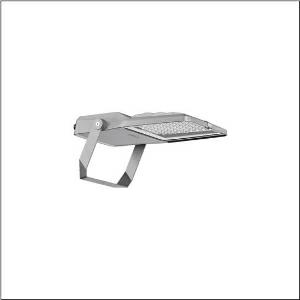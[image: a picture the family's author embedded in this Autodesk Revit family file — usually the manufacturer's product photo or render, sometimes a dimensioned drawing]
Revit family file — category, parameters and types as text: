
# Revit family: floodlight_fl_21_iq_mini___pl52_5xa7772b2d1a_4cc7
name_source: partatom
category: Lighting Fixtures
units: mm (PartAtom-declared; Revit-internal decimal feet)

## family parameters
Cut with Voids When Loaded = No
Host = Face
Light Source = No
Part Type = Normal
Room Calculation Point = No
Round Connector Dimension = Use Diameter
Shared = No

## types (1)
- --- (1 x LED, 6240 lm, 45.5 W, 3000K)
    Apparent Load = 46 VA
    CIE Flux Codes = 26 60 98 100 100
    Color Rendering = 70
    Color Temperature = 3000K
    Default Elevation = 1800 mm
    Description = Floodlight FL 21 iQ mini, floodlight, primary light control with lens, of PMMA, primary optical cover: protective disc, of toughened safety glass, transparent, light distribution: PL52, light emission: direct distribution, installation type: surface-mounted, LED, High Power LED, rated luminous flux: 6.240lm, luminous efficacy: 137lm/W, light colour: 730, colour temperature: 3000K, control gear: iQ Street-Remote/DALI, control: Street-Remote, Auto-Match, Temp-Guard, Night-Set, Smart-Wire, Desk-Remote (wireless, voltage-free reading and setting of iQ features in the workshop via application-optimized NFC function/RFID function), optimised constant luminous flux control (CLO 2.0), with terminal, 6-pole, mains connection: 220..240V, AC, 50/60Hz, start of lifetime: 46W, end of service life: 48W, reduction: 22W, luminaire housing, of diecast aluminium, powder-coated, Siteco® metallic grey (DB 702S), corrosivity category C5 mid according to DIN EN ISO 12944, suitable for swimming pools, chlorine-resistant, sealing non-destructively replaceable, mounting bracket, of steel, galvanised, powder-coated, Siteco® metallic grey (DB 702S), protection rating (complete): IP66, insulation class (complete): insulation class II (safety insulation), certification: CE, ENEC, VDE, protection symbol: D, impact resistance: IK08, permissible operating ambient temperature: -40..+40°C, permissible operating ambient temperature for outdoor applications: -40..+50°C, standard: DIN EN 12944, LABS conformity tested according to VDMA 24364:2018-05, packaging unit: 1 piece

Light Distribution: PL52
    Height = 70 mm
    Lamp = 1 x LED
    Lamp Light Flux = 6240 lm
    Lamp Power = 45.5 W
    Lamp count = 1
    Length = 485 mm
    Luminous efficacy = 137 lm/W
    Manufacturer = Siteco
    ModVariant = No
    Model = 5XA7772B2D1A
    Number of Poles = 1
    OnlyDefault = Yes
    Power Factor = 1
    Product Name = Floodlight FL 21 iQ mini | PL52
    Product group = floodlight | pylon annexe
    ProductGroupID = 6201
    Protection Class = Protection class II
    Protection Degree = IP 66
    RLX_Detail_Level = 1
    RLX_Emergency_Light_Flux = 0 lm
    RLX_Emergency_Type = 0
    RLX_Emergency_Type_DB = No
    RlxData = <blob elided: 96333 chars, md5=1efc46d8>
    Socket = socket
    Standby Power = 0 W
    System Light Flux = 6240 lm
    System Power = 46 W
    Type Comments = factory setting: luminous flux: 100 % | dim-lin: 254 | 463 mA
    Type Image = l_1006845.jpg
    URL = http://relux.com
    VarID = @adj_186373
    Voltage = 0 V
    Weight = 0.00 kg
    Width = 337 mm

## geometry (parser evidence)
native form markers: Blend x4, Sweep x12
no freeform markers — native parametric forms only
